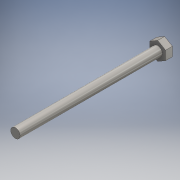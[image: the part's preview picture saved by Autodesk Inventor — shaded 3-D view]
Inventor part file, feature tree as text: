
AUTODESK INVENTOR PART (.ipt)
format: ipt  version: 2016 (Build 200138000, 138)  size: 123,904 bytes
history: native  units: mm
features: extrude x2, sketch x2
ambient origin geometry x8: Origin, YZ Plane, XZ Plane, XY Plane, X Axis, Y Axis, Z Axis, Center Point
bodies: Solid1 (feature_tree)
feature tree (4):
  extrude  "Extrusion1"  Depth=95.0mm TaperAngle=0.0deg
  extrude  "Extrusion2"  Depth=4.4mm TaperAngle=0.0deg
  sketch  "Sketch1"  dims[d0=6.0mm d1=95.0mm d2=0.0mm]
  sketch  "Sketch2"  dims[d3=10.0mm d4=4.4mm d5=0.0mm]
